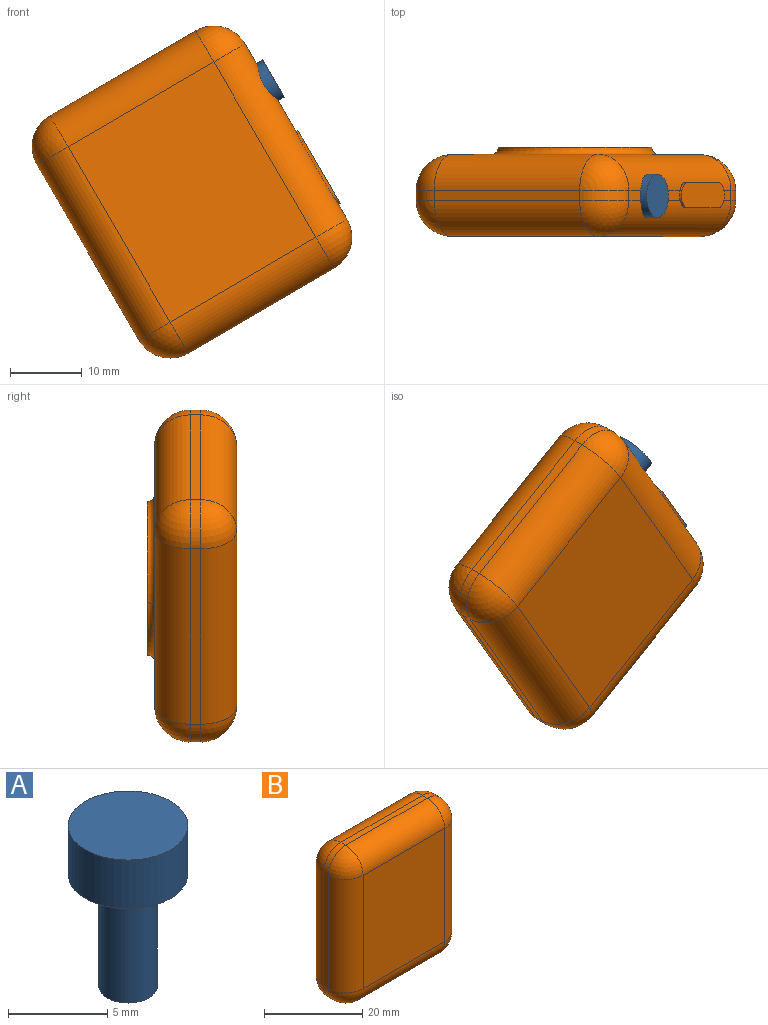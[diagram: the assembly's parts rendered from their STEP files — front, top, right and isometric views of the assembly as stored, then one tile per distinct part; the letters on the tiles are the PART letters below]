
ASSEMBLY  parts=2 mates=1
PART A: 5 faces, bbox 6x6x9.9 mm
  f0: cylinder r=1.48mm len=6.9mm, axis (0,0,-1), area 64mm2, adj f1,f4
  f1: plane 2.95x2.95mm, normal (0,0,-1), area 6.8mm2, adj f0
  f2: cylinder r=3.01mm len=6.03mm, axis (0,0,-1), area 56.8mm2, adj f3,f4
  f3: plane 6.03x6.03mm, normal (0,0,1), area 28.5mm2, adj f2
  f4: plane 6.03x6.03mm, normal (0,0,-1), area 21.7mm2, adj f0,f2
PART B: 45 faces, bbox 33.7x13.1x38.2 mm
  f0: plane 3.29x1.4mm, normal (1,0,0), area 4.5mm2, adj f11,f15,f16,f42
  f1: plane 2.51x1.4mm, normal (1,0,0), area 3.4mm2, adj f8,f11,f15,f34,f38,f39
  f2: plane 23.43x1.4mm, normal (0,0,1), area 32.8mm2, adj f16,f21,f24,f27
  f3: plane 28.2x1.4mm, normal (-1,0,0), area 39.5mm2, adj f13,f22,f23,f27
  f4: plane 23.43x1.4mm, normal (0,0,-1), area 32.8mm2, adj f8,f12,f13,f14
  f5: plane 5.09x1.4mm, normal (1,0,0), area 6.9mm2, adj f11,f15,f32,f37,f40,f42
  f6: plane 28.2x23.43mm, normal (0,-1,0), area 660.6mm2, adj f11,f12,f21,f22
  f7: plane 28.2x23.43mm, normal (0,1,0), area 232.7mm2, adj f14,f15,f23,f24,f30
  f8: cylinder r=5mm len=5mm, axis (0,-1,0), area 11mm2, adj f1,f4,f9,f10
  f9: sphere r=5mm, area 39.3mm2, adj f8,f11,f12
  f10: sphere r=5mm, area 39.3mm2, adj f8,f14,f15
  f11: cylinder r=5mm len=28.2mm, axis (0,0,-1), area 199.7mm2, adj f0,f1,f5,f6,f9,f17,f33,f37
  f12: cylinder r=5mm len=23.43mm, axis (-1,0,0), area 184mm2, adj f4,f6,f9,f18
  f13: cylinder r=5mm len=5mm, axis (0,1,0), area 11mm2, adj f3,f4,f18,f19
  f14: cylinder r=5mm len=23.43mm, axis (1,0,0), area 184mm2, adj f4,f7,f10,f19
  f15: cylinder r=5mm len=28.2mm, axis (0,0,1), area 199.8mm2, adj f0,f1,f5,f7,f10,f20,f35,f39
  f16: cylinder r=5mm len=5mm, axis (0,1,0), area 11mm2, adj f0,f2,f17,f20
  f17: sphere r=5mm, area 39.3mm2, adj f11,f16,f21
  f18: sphere r=5mm, area 39.3mm2, adj f12,f13,f22
  f19: sphere r=5mm, area 39.3mm2, adj f13,f14,f23
  f20: sphere r=5mm, area 39.3mm2, adj f15,f16,f24
  f21: cylinder r=5mm len=23.43mm, axis (1,0,0), area 184mm2, adj f2,f6,f17,f25
  f22: cylinder r=5mm len=28.2mm, axis (0,0,1), area 221.5mm2, adj f3,f6,f18,f25
  f23: cylinder r=5mm len=28.2mm, axis (0,0,-1), area 220.9mm2, adj f3,f7,f19,f26,f31
  f24: cylinder r=5mm len=23.43mm, axis (-1,0,0), area 184mm2, adj f2,f7,f20,f26
  f25: sphere r=5mm, area 39.3mm2, adj f21,f22,f27
  f26: sphere r=5mm, area 39.3mm2, adj f23,f24,f27
  f27: cylinder r=5mm len=5mm, axis (0,-1,0), area 11mm2, adj f2,f3,f25,f26
  f28: cylinder r=10.68mm len=4.28mm, axis (0,-1,0), area 0mm2, adj f29,f31
  f29: plane 21.36x21.36mm, normal (0,1,0), area 358.5mm2, adj f28,f30
  f30: torus R=11.68mm, axis (0,-1,0), area 102mm2, adj f7,f29,f31
  f31: bspline ~6.38x1.47mm, area 6.9mm2, adj f23,f28,f30
  f32: plane 0.3x0.13mm, normal (0,0,1), area 0mm2, adj f5,f36,f37,f40
  f33: plane 8.38x0.41mm, normal (0,-1,0), area 3.4mm2, adj f11,f36,f37,f38
  f34: plane 0.3x0.13mm, normal (0,0,-1), area 0mm2, adj f1,f36,f38,f39
  f35: plane 8.38x0.43mm, normal (0,1,0), area 3.6mm2, adj f15,f36,f39,f40
  f36: plane 11.78x3.53mm, normal (1,0,0), area 39.1mm2, adj f32,f33,f34,f35,f37,f38,f39,f40
  f37: cylinder r=1.7mm len=1.7mm, axis (1,0,0), area 0.9mm2, adj f5,f11,f32,f33,f36
  f38: cylinder r=1.7mm len=1.7mm, axis (-1,0,0), area 0.9mm2, adj f1,f11,f33,f34,f36
  f39: cylinder r=1.7mm len=1.7mm, axis (1,0,0), area 0.9mm2, adj f1,f15,f34,f35,f36
  f40: cylinder r=1.7mm len=1.7mm, axis (-1,0,0), area 0.9mm2, adj f5,f15,f32,f35,f36
  f41: plane 6.01x6.01mm, normal (1,0,0), area 21.5mm2, adj f42,f44
  f42: cylinder r=3.01mm len=6.01mm, axis (1,0,0), area 33.2mm2, adj f0,f5,f11,f15,f41
  f43: plane 2.96x2.96mm, normal (1,0,0), area 6.9mm2, adj f44
  f44: cylinder r=1.48mm len=5mm, axis (1,0,0), area 46.6mm2, adj f41,f43
PLACE A rot(axis=(-0.5,0,-0.87),180deg) t=(30.13,-29.43,38.88)mm
PLACE B rot(axis=(0,-1,0),30.2deg) t=(33.98,-21.1,25.51)mm
MATE revolute A.f0 <-> B.f42  axis (-0.86,0,-0.5) through (39.63,-26.88,36.28)mm
